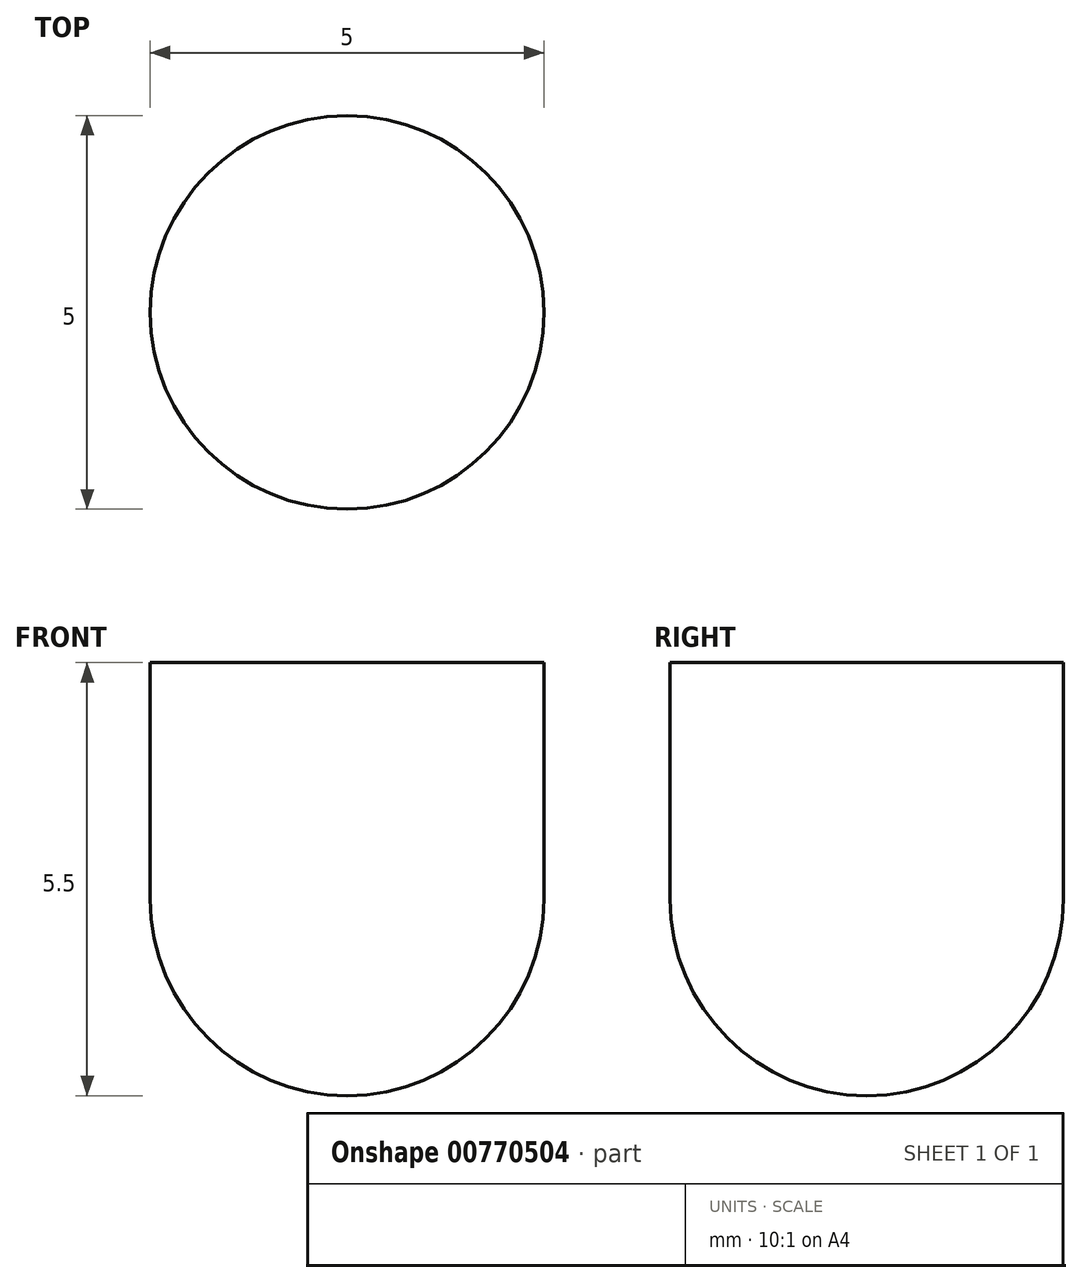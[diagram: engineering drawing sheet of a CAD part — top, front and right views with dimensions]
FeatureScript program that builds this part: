
annotation { "Feature Type Name" : "Feature", "Feature Type Description" : "" }
export const myFeature = defineFeature(function(context is Context, id is Id, definition is map)
    precondition{}
    {
        {
            var Q0;
            Q0=qCreatedBy(makeId("Top.planeOp"),FACE);
            var sketch = newSketch(context, id + "F0", { "sketchPlane" : qUnion([Q0])});
            skCircle(sketch, "E0", {"center": v(0, 0) * mm, "radius": 2.5 * mm});
            skSolve(sketch);
        }
        {
            var Q0;
            Q0=makeQuery(id+"F0.imprint","IMPRINT",FACE,{"disambiguationData":[TD([[makeQuery(id+"F0.imprint","IMPRINT",EDGE,{"derivedFrom":sQuery(id+"F0.wireOp",EDGE,"E0")}),1.0]])]});
            var Q1;
            Q1=sQuery(id+"F0.wireOp",EDGE,"E0");
            extrude(context, id + "F1", {"entities" : qUnion([Q0]), "surfaceEntities" : qUnion([Q1]), "depth" : 3 * mm, "offsetDistance" : 25 * mm});
        }
        {
            var Q0;
            Q0=qCreatedBy(makeId("Front.planeOp"),FACE);
            var sketch = newSketch(context, id + "F2", { "sketchPlane" : qUnion([Q0])});
            skArc(sketch, "E1", {"start": v(-2.5, 0) * mm, "mid": v(0, -2.5) * mm, "end": v(2.5, 0) * mm});
            skLineSegment(sketch, "E2", {"start": v(-2.5, 0) * mm, "end": v(2.5, 0) * mm});
            skSolve(sketch);
        }
        {
            var Q0;
            Q0=makeQuery(id+"F2.imprint","IMPRINT",FACE,{"disambiguationData":[TD([[makeQuery(id+"F2.imprint","IMPRINT",EDGE,{"derivedFrom":sQuery(id+"F2.wireOp",EDGE,"E1")}),1.0]])]});
            var Q1;
            Q1=sQuery(id+"F2.wireOp",EDGE,"E2");
            revolve(context, id + "F3", {"operationType" : NewBodyOperationType.ADD, "surfaceOperationType" : NewSurfaceOperationType.NEW, "entities" : qUnion([Q0]), "axis" : qUnion([Q1]), "revolveType" : RevolveType.FULL});
        }
    });
